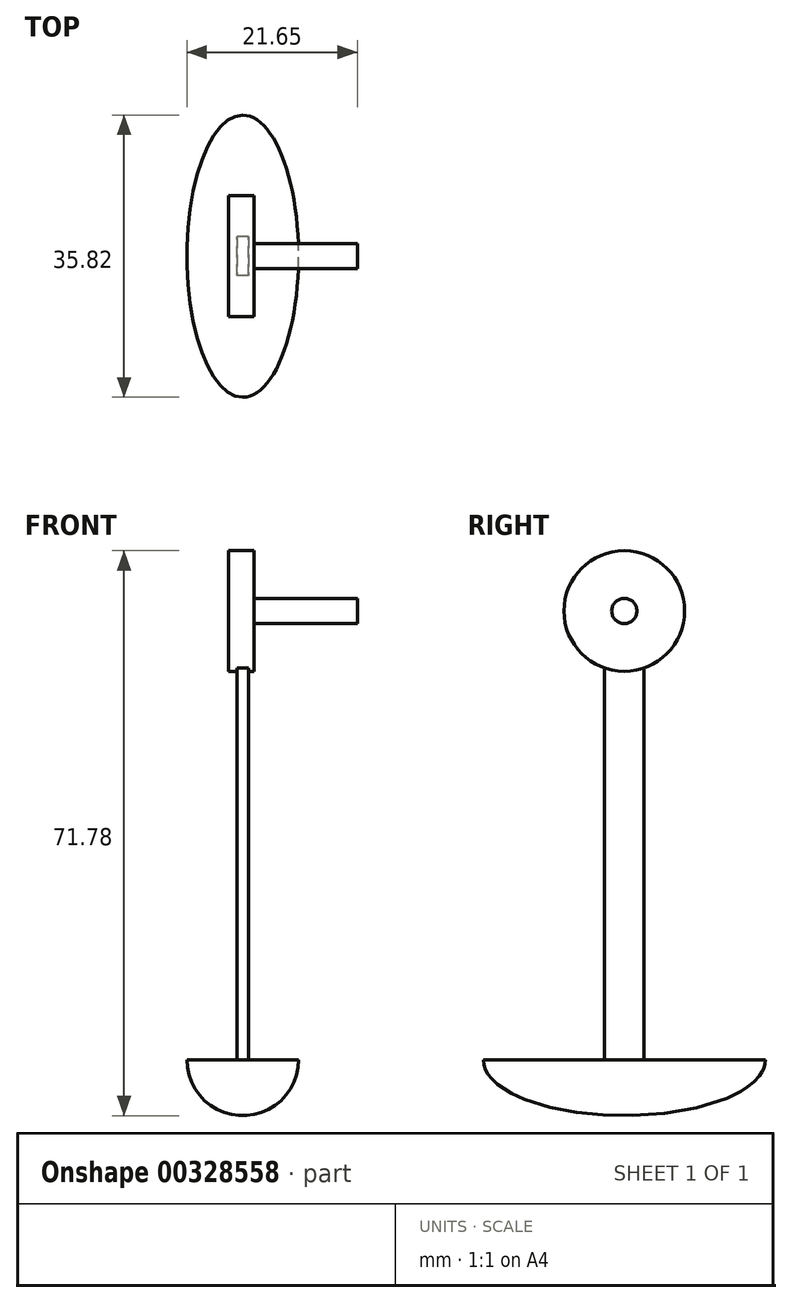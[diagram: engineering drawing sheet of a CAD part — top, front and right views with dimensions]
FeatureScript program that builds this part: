
annotation { "Feature Type Name" : "Feature", "Feature Type Description" : "" }
export const myFeature = defineFeature(function(context is Context, id is Id, definition is map)
    precondition{}
    {
        {
            var Q0;
            Q0=qCreatedBy(makeId("Front.planeOp"),FACE);
            var sketch = newSketch(context, id + "F0", { "sketchPlane" : qUnion([Q0])});
            skLineSegment(sketch, "E0.bottom", {"start": v(0, 67.45) * mm, "end": v(-13.11, 67.45) * mm});
            skLineSegment(sketch, "E0.left", {"start": v(0, 67.45) * mm, "end": v(0, 65.85) * mm});
            skLineSegment(sketch, "E1.top", {"start": v(-13.11, 73.5) * mm, "end": v(-16.36, 73.5) * mm});
            skLineSegment(sketch, "E1.left", {"start": v(-13.11, 65.85) * mm, "end": v(-13.11, 73.5) * mm});
            skLineSegment(sketch, "E1.right", {"start": v(-16.36, 65.85) * mm, "end": v(-16.36, 73.5) * mm});
            skPoint(sketch, "E1.middle", {"position": v(-13.85, 37.33) * mm});
            skLineSegment(sketch, "E2.bottom", {"start": v(-13.85, 8.82) * mm, "end": v(-15.27, 8.82) * mm});
            skLineSegment(sketch, "E2.left", {"start": v(-13.85, 8.82) * mm, "end": v(-13.85, 65.85) * mm});
            skLineSegment(sketch, "E2.right", {"start": v(-15.27, 8.82) * mm, "end": v(-15.27, 65.85) * mm});
            skPoint(sketch, "E2.middle", {"position": v(-13.85, 41.97) * mm});
            skPoint(sketch, "E3.endSnap0", {"position": v(-13.11, 65.85) * mm});
            skLineSegment(sketch, "E4", {"start": v(-16.36, 65.85) * mm, "end": v(0, 65.85) * mm});
            skLineSegment(sketch, "E5", {"start": v(-15.27, 65.85) * mm, "end": v(-13.85, 65.85) * mm});
            skSolve(sketch);
        }
        {
            var Q0;
            {var subQ3=sQuery(id+"F0.wireOp",EDGE,"E1.top");Q0=makeQuery(id+"F0.imprint","IMPRINT",FACE,{"disambiguationData":[TD([[makeQuery(id+"F0.imprint","IMPRINT",EDGE,{"derivedFrom":subQ3}),1.0]])]});}
            var Q1;
            {var subQ0=sQuery(id+"F0.wireOp",EDGE,"E0.bottom");Q1=makeQuery(id+"F0.imprint","IMPRINT",FACE,{"disambiguationData":[TD([[makeQuery(id+"F0.imprint","IMPRINT",EDGE,{"derivedFrom":subQ0}),1.0]])]});}
            var Q2;
            Q2=sQuery(id+"F0.wireOp",EDGE,"E4");
            revolve(context, id + "F1", {"entities" : qUnion([Q0, Q1]), "axis" : qUnion([Q2]), "revolveType" : RevolveType.FULL});
        }
        {
            var Q0;
            Q0=makeQuery(id+"F0.imprint","IMPRINT",FACE,{"disambiguationData":[TD([[makeQuery(id+"F0.imprint","IMPRINT",EDGE,{"derivedFrom":sQuery(id+"F0.wireOp",EDGE,"E2.bottom")}),-1.0]])]});
            extrude(context, id + "F2", {"entities" : qUnion([Q0]), "operationType" : NewBodyOperationType.ADD, "endBound" : BoundingType.SYMMETRIC, "depth" : 5 * mm});
        }
        {
            var Q0;
            Q0=makeQuery(id+"F2.opExtrude","SWEPT_FACE",FACE,{"disambiguationData":[OSD([sQuery(id+"F0.wireOp",EDGE,"E2.bottom")])]});
            cPlane(context, id + "F3", {"entities" : qUnion([Q0]), "cplaneType" : CPlaneType.OFFSET, "offset" : 0 * mm, "width" : 150 * mm, "height" : 150 * mm});
        }
        {
            var Q0;
            Q0=qCreatedBy(id+"F3.planeOp",FACE);
            var sketch = newSketch(context, id + "F4", { "sketchPlane" : qUnion([Q0])});
            skLineSegment(sketch, "E6", {"start": v(-13.7, 0) * mm, "end": v(-15.96, 0) * mm, "construction": true});
            skLineSegment(sketch, "E7", {"start": v(-14.56, -2.5) * mm, "end": v(-14.56, 2.5) * mm, "construction": true});
            skEllipticalArc(sketch, "E8", {});
            skLineSegment(sketch, "E9", {"start": v(-14.56, 2.5) * mm, "end": v(-14.56, 17.91) * mm});
            skLineSegment(sketch, "E10", {"start": v(-14.56, 17.91) * mm, "end": v(-14.56, -17.91) * mm});
            const initialGuessF4  = {"E8": [-0.014556926675140858, 0, 0, -1, 0.017911046743392944, 0.007092243835203478, 3.141592653589793, 0]};
            skSetInitialGuess(sketch, initialGuessF4);
            skSolve(sketch);
        }
        {
            var Q0;
            {var subQ0=sQuery(id+"F4.wireOp",EDGE,"E8");Q0=makeQuery(id+"F4.imprint","IMPRINT",FACE,{"disambiguationData":[TD([[makeQuery(id+"F4.imprint","IMPRINT",EDGE,{"derivedFrom":subQ0}),1.0]])]});}
            var Q1;
            Q1=sQuery(id+"F4.wireOp",EDGE,"E10");
            revolve(context, id + "F5", {"operationType" : NewBodyOperationType.ADD, "entities" : qUnion([Q0]), "axis" : qUnion([Q1]), "revolveType" : RevolveType.ONE_DIRECTION, "oppositeDirection" : true, "angle" : 180 * degree});
        }
    });
